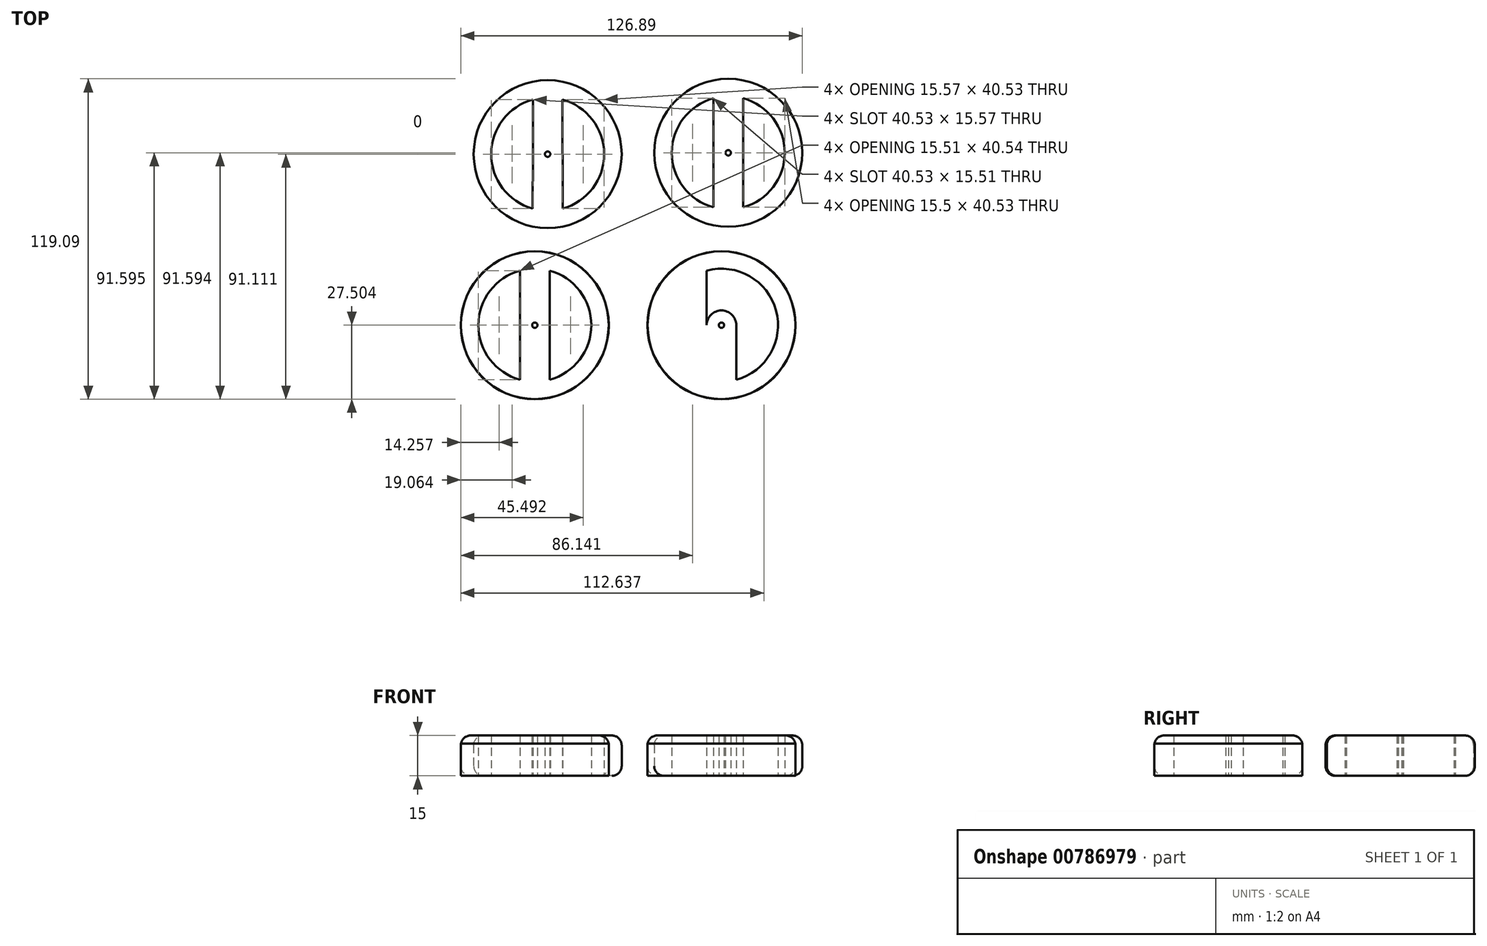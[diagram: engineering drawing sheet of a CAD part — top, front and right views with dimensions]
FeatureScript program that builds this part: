
annotation { "Feature Type Name" : "Feature", "Feature Type Description" : "" }
export const myFeature = defineFeature(function(context is Context, id is Id, definition is map)
    precondition{}
    {
        {
            var Q0;
            Q0=qCreatedBy(makeId("Top.planeOp"),FACE);
            var sketch = newSketch(context, id + "F0", { "sketchPlane" : qUnion([Q0])});
            skCircle(sketch, "E0", {"center": v(-34.05, 31.81) * mm, "radius": 27.5 * mm});
            skCircle(sketch, "E1", {"center": v(33.06, 32.31) * mm, "radius": 27.5 * mm});
            skCircle(sketch, "E2", {"center": v(30.54, -31.78) * mm, "radius": 27.5 * mm});
            skCircle(sketch, "E3", {"center": v(-38.83, -31.78) * mm, "radius": 27.5 * mm});
            skCircle(sketch, "E4", {"center": v(-38.83, -31.78) * mm, "radius": 21 * mm});
            skCircle(sketch, "E5", {"center": v(30.54, -31.78) * mm, "radius": 21 * mm});
            skCircle(sketch, "E6", {"center": v(33.06, 32.31) * mm, "radius": 21 * mm});
            skCircle(sketch, "E7", {"center": v(33.06, 32.31) * mm, "radius": 1 * mm});
            skCircle(sketch, "E8", {"center": v(33.06, 32.31) * mm, "radius": 5.5 * mm});
            skCircle(sketch, "E9", {"center": v(-34.05, 31.81) * mm, "radius": 21 * mm});
            skCircle(sketch, "E10", {"center": v(-34.05, 31.81) * mm, "radius": 5.5 * mm});
            skCircle(sketch, "E11", {"center": v(-38.83, -31.78) * mm, "radius": 1 * mm});
            skCircle(sketch, "E12", {"center": v(-38.83, -31.78) * mm, "radius": 5.5 * mm});
            skCircle(sketch, "E13", {"center": v(30.54, -31.78) * mm, "radius": 1 * mm});
            skCircle(sketch, "E14", {"center": v(30.54, -31.78) * mm, "radius": 5.5 * mm});
            skCircle(sketch, "E15", {"center": v(-34.05, 31.81) * mm, "radius": 1 * mm});
            skLineSegment(sketch, "E16", {"start": v(-39.48, 32.7) * mm, "end": v(-39.48, 52.1) * mm});
            skLineSegment(sketch, "E17", {"start": v(-39.48, 52.1) * mm, "end": v(-39.62, 11.56) * mm});
            skLineSegment(sketch, "E18", {"start": v(-28.48, 11.56) * mm, "end": v(-28.62, 52.1) * mm});
            skLineSegment(sketch, "E19", {"start": v(27.56, 32.58) * mm, "end": v(27.56, 52.58) * mm});
            skLineSegment(sketch, "E20", {"start": v(27.56, 52.58) * mm, "end": v(27.55, 12.05) * mm});
            skLineSegment(sketch, "E21", {"start": v(-44.32, -31.53) * mm, "end": v(-44.32, -11.5) * mm});
            skLineSegment(sketch, "E22", {"start": v(-44.32, -31.53) * mm, "end": v(-44.32, -52.04) * mm});
            skLineSegment(sketch, "E23", {"start": v(-33.33, -31.53) * mm, "end": v(-33.33, -52.04) * mm});
            skLineSegment(sketch, "E24", {"start": v(-33.33, -31.53) * mm, "end": v(-33.33, -11.5) * mm});
            skLineSegment(sketch, "E25", {"start": v(25.04, -31.78) * mm, "end": v(25.04, -11.51) * mm});
            skLineSegment(sketch, "E26", {"start": v(25.04, -11.51) * mm, "end": v(25.04, -52.04) * mm});
            skLineSegment(sketch, "E27", {"start": v(36.04, -31.78) * mm, "end": v(36.04, -11.51) * mm});
            skLineSegment(sketch, "E28", {"start": v(36.04, -11.51) * mm, "end": v(36.04, -52.04) * mm});
            skLineSegment(sketch, "E29", {"start": v(38.56, 32.31) * mm, "end": v(38.56, 12.05) * mm});
            skLineSegment(sketch, "E30", {"start": v(38.56, 32.31) * mm, "end": v(38.56, 52.58) * mm});
            skSolve(sketch);
        }
        {
            var Q0;
            Q0=makeQuery(id+"F0.imprint","IMPRINT",FACE,{"disambiguationData":[TD([[makeQuery(id+"F0.imprint","IMPRINT",EDGE,{"derivedFrom":sQuery(id+"F0.wireOp",EDGE,"E0")}),1.0]])]});
            var Q1;
            Q1=makeQuery(id+"F0.imprint","IMPRINT",FACE,{"disambiguationData":[TD([[makeQuery(id+"F0.imprint","IMPRINT",EDGE,{"derivedFrom":sQuery(id+"F0.wireOp",EDGE,"E1")}),1.0]])]});
            var Q2;
            {var subQ0=sQuery(id+"F0.wireOp",EDGE,"E17");var subQ1=sQuery(id+"F0.wireOp",EDGE,"E9");var subQ2=makeQuery(id+"F0.imprint","INTERSECT",VERTEX,{"derivedFrom":[subQ1,subQ0]});Q2=makeQuery(id+"F0.imprint","IMPRINT",FACE,{"disambiguationData":[TD([[makeQuery(id+"F0.imprint","IMPRINT",EDGE,{"disambiguationData":[TD([[subQ2,-1.0]])],"derivedFrom":subQ1}),1.0]])]});}
            var Q3;
            Q3=makeQuery(id+"F0.imprint","IMPRINT",FACE,{"disambiguationData":[TD([[makeQuery(id+"F0.imprint","IMPRINT",EDGE,{"derivedFrom":sQuery(id+"F0.wireOp",EDGE,"E15")}),-1.0]])]});
            var Q4;
            {var subQ0=sQuery(id+"F0.wireOp",EDGE,"E16");Q4=makeQuery(id+"F0.imprint","IMPRINT",FACE,{"disambiguationData":[TD([[makeQuery(id+"F0.imprint","IMPRINT",EDGE,{"derivedFrom":subQ0}),-1.0]])]});}
            var Q5;
            Q5=makeQuery(id+"F0.imprint","IMPRINT",FACE,{"disambiguationData":[TD([[makeQuery(id+"F0.imprint","IMPRINT",EDGE,{"derivedFrom":sQuery(id+"F0.wireOp",EDGE,"E7")}),-1.0]])]});
            var Q6;
            {var subQ0=sQuery(id+"F0.wireOp",EDGE,"E19");Q6=makeQuery(id+"F0.imprint","IMPRINT",FACE,{"disambiguationData":[TD([[makeQuery(id+"F0.imprint","IMPRINT",EDGE,{"derivedFrom":subQ0}),-1.0]])]});}
            var Q7;
            {var subQ0=sQuery(id+"F0.wireOp",EDGE,"E20");var subQ1=sQuery(id+"F0.wireOp",EDGE,"E6");var subQ2=makeQuery(id+"F0.imprint","INTERSECT",VERTEX,{"derivedFrom":[subQ1,subQ0]});Q7=makeQuery(id+"F0.imprint","IMPRINT",FACE,{"disambiguationData":[TD([[makeQuery(id+"F0.imprint","IMPRINT",EDGE,{"disambiguationData":[TD([[subQ2,-1.0]])],"derivedFrom":subQ1}),1.0]])]});}
            extrude(context, id + "F1", {"entities" : qUnion([Q0, Q1, Q2, Q3, Q4, Q5, Q6, Q7]), "depth" : 15 * mm, "offsetDistance" : 25 * mm});
        }
        {
            var Q0;
            Q0=makeQuery(id+"F1.opExtrude","CAP_EDGE",EDGE,{"disambiguationData":[OSD([sQuery(id+"F0.wireOp",EDGE,"E0")])],"isStart":false});
            var Q1;
            Q1=makeQuery(id+"F1.opExtrude","CAP_EDGE",EDGE,{"disambiguationData":[OSD([sQuery(id+"F0.wireOp",EDGE,"E0")])],"isStart":true});
            fillet(context, id + "F2", {"entities" : qUnion([Q0, Q1]), "radius" : 3.62 * mm, "tangentPropagation" : true, "allowEdgeOverflow" : false});
        }
        {
            var Q0;
            Q0=makeQuery(id+"F1.opExtrude","CAP_EDGE",EDGE,{"disambiguationData":[OSD([sQuery(id+"F0.wireOp",EDGE,"E1")])],"isStart":false});
            var Q1;
            Q1=makeQuery(id+"F1.opExtrude","CAP_EDGE",EDGE,{"disambiguationData":[OSD([sQuery(id+"F0.wireOp",EDGE,"E1")])],"isStart":true});
            fillet(context, id + "F3", {"entities" : qUnion([Q0, Q1]), "radius" : 3.62 * mm, "tangentPropagation" : true, "allowEdgeOverflow" : false});
        }
        {
            var Q0;
            {var subQ0=sQuery(id+"F0.wireOp",EDGE,"E26");var subQ1=sQuery(id+"F0.wireOp",EDGE,"E5");var subQ2=makeQuery(id+"F0.imprint","INTERSECT",VERTEX,{"disambiguationData":[OD(0.0)],"derivedFrom":[subQ1,subQ0]});Q0=makeQuery(id+"F0.imprint","IMPRINT",FACE,{"disambiguationData":[TD([[makeQuery(id+"F0.imprint","IMPRINT",EDGE,{"disambiguationData":[TD([[subQ2,1.0]])],"derivedFrom":subQ1}),1.0]])]});}
            var Q1;
            {var subQ0=sQuery(id+"F0.wireOp",EDGE,"E26");var subQ1=sQuery(id+"F0.wireOp",EDGE,"E5");var subQ2=makeQuery(id+"F0.imprint","INTERSECT",VERTEX,{"disambiguationData":[OD(1.0)],"derivedFrom":[subQ1,subQ0]});Q1=makeQuery(id+"F0.imprint","IMPRINT",FACE,{"disambiguationData":[TD([[makeQuery(id+"F0.imprint","IMPRINT",EDGE,{"disambiguationData":[TD([[subQ2,-1.0]])],"derivedFrom":subQ1}),1.0]])]});}
            var Q2;
            Q2=makeQuery(id+"F0.imprint","IMPRINT",FACE,{"disambiguationData":[TD([[makeQuery(id+"F0.imprint","IMPRINT",EDGE,{"derivedFrom":sQuery(id+"F0.wireOp",EDGE,"E13")}),-1.0]])]});
            var Q3;
            Q3=makeQuery(id+"F0.imprint","IMPRINT",FACE,{"disambiguationData":[TD([[makeQuery(id+"F0.imprint","IMPRINT",EDGE,{"derivedFrom":sQuery(id+"F0.wireOp",EDGE,"E2")}),1.0]])]});
            var Q4;
            {var subQ0=sQuery(id+"F0.wireOp",EDGE,"E22");var subQ1=sQuery(id+"F0.wireOp",EDGE,"E4");var subQ2=makeQuery(id+"F0.imprint","INTERSECT",VERTEX,{"derivedFrom":[subQ1,subQ0]});Q4=makeQuery(id+"F0.imprint","IMPRINT",FACE,{"disambiguationData":[TD([[makeQuery(id+"F0.imprint","IMPRINT",EDGE,{"disambiguationData":[TD([[subQ2,-1.0]])],"derivedFrom":subQ1}),1.0]])]});}
            var Q5;
            Q5=makeQuery(id+"F0.imprint","IMPRINT",FACE,{"disambiguationData":[TD([[makeQuery(id+"F0.imprint","IMPRINT",EDGE,{"derivedFrom":sQuery(id+"F0.wireOp",EDGE,"E11")}),-1.0]])]});
            var Q6;
            {var subQ0=sQuery(id+"F0.wireOp",EDGE,"E21");Q6=makeQuery(id+"F0.imprint","IMPRINT",FACE,{"disambiguationData":[TD([[makeQuery(id+"F0.imprint","IMPRINT",EDGE,{"derivedFrom":subQ0}),-1.0]])]});}
            var Q7;
            Q7=makeQuery(id+"F0.imprint","IMPRINT",FACE,{"disambiguationData":[TD([[makeQuery(id+"F0.imprint","IMPRINT",EDGE,{"derivedFrom":sQuery(id+"F0.wireOp",EDGE,"E3")}),1.0]])]});
            extrude(context, id + "F4", {"entities" : qUnion([Q0, Q1, Q2, Q3, Q4, Q5, Q6, Q7]), "operationType" : NewBodyOperationType.ADD, "depth" : 12 * mm, "offsetDistance" : 25 * mm});
        }
        {
            var Q0;
            Q0=makeQuery(id+"F0.imprint","IMPRINT",FACE,{"disambiguationData":[TD([[makeQuery(id+"F0.imprint","IMPRINT",EDGE,{"derivedFrom":sQuery(id+"F0.wireOp",EDGE,"E2")}),1.0]])]});
            var Q1;
            {var subQ0=sQuery(id+"F0.wireOp",EDGE,"E26");var subQ1=sQuery(id+"F0.wireOp",EDGE,"E5");var subQ2=makeQuery(id+"F0.imprint","INTERSECT",VERTEX,{"disambiguationData":[OD(1.0)],"derivedFrom":[subQ1,subQ0]});Q1=makeQuery(id+"F0.imprint","IMPRINT",FACE,{"disambiguationData":[TD([[makeQuery(id+"F0.imprint","IMPRINT",EDGE,{"disambiguationData":[TD([[subQ2,-1.0]])],"derivedFrom":subQ1}),1.0]])]});}
            var Q2;
            Q2=makeQuery(id+"F0.imprint","IMPRINT",FACE,{"disambiguationData":[TD([[makeQuery(id+"F0.imprint","IMPRINT",EDGE,{"derivedFrom":sQuery(id+"F0.wireOp",EDGE,"E13")}),-1.0]])]});
            var Q3;
            {var subQ0=sQuery(id+"F0.wireOp",EDGE,"E26");var subQ1=sQuery(id+"F0.wireOp",EDGE,"E5");var subQ2=makeQuery(id+"F0.imprint","INTERSECT",VERTEX,{"disambiguationData":[OD(0.0)],"derivedFrom":[subQ1,subQ0]});Q3=makeQuery(id+"F0.imprint","IMPRINT",FACE,{"disambiguationData":[TD([[makeQuery(id+"F0.imprint","IMPRINT",EDGE,{"disambiguationData":[TD([[subQ2,1.0]])],"derivedFrom":subQ1}),1.0]])]});}
            var Q4;
            {var subQ0=sQuery(id+"F0.wireOp",EDGE,"E21");Q4=makeQuery(id+"F0.imprint","IMPRINT",FACE,{"disambiguationData":[TD([[makeQuery(id+"F0.imprint","IMPRINT",EDGE,{"derivedFrom":subQ0}),-1.0]])]});}
            var Q5;
            Q5=makeQuery(id+"F0.imprint","IMPRINT",FACE,{"disambiguationData":[TD([[makeQuery(id+"F0.imprint","IMPRINT",EDGE,{"derivedFrom":sQuery(id+"F0.wireOp",EDGE,"E3")}),1.0]])]});
            var Q6;
            Q6=makeQuery(id+"F0.imprint","IMPRINT",FACE,{"disambiguationData":[TD([[makeQuery(id+"F0.imprint","IMPRINT",EDGE,{"derivedFrom":sQuery(id+"F0.wireOp",EDGE,"E11")}),-1.0]])]});
            var Q7;
            {var subQ0=sQuery(id+"F0.wireOp",EDGE,"E22");var subQ1=sQuery(id+"F0.wireOp",EDGE,"E4");var subQ2=makeQuery(id+"F0.imprint","INTERSECT",VERTEX,{"derivedFrom":[subQ1,subQ0]});Q7=makeQuery(id+"F0.imprint","IMPRINT",FACE,{"disambiguationData":[TD([[makeQuery(id+"F0.imprint","IMPRINT",EDGE,{"disambiguationData":[TD([[subQ2,-1.0]])],"derivedFrom":subQ1}),1.0]])]});}
            extrude(context, id + "F5", {"entities" : qUnion([Q0, Q1, Q2, Q3, Q4, Q5, Q6, Q7]), "depth" : 15 * mm, "offsetDistance" : 25 * mm});
        }
        {
            var Q0;
            Q0=makeQuery(id+"F5.opExtrude","CAP_EDGE",EDGE,{"disambiguationData":[OSD([sQuery(id+"F0.wireOp",EDGE,"E3")])],"isStart":false});
            var Q1;
            Q1=makeQuery(id+"F5.opExtrude","CAP_EDGE",EDGE,{"disambiguationData":[OSD([sQuery(id+"F0.wireOp",EDGE,"E3")])],"isStart":true});
            fillet(context, id + "F6", {"entities" : qUnion([Q0, Q1]), "radius" : 3.62 * mm, "tangentPropagation" : true, "allowEdgeOverflow" : false});
        }
        {
            var Q0;
            Q0=makeQuery(id+"F5.opExtrude","CAP_EDGE",EDGE,{"disambiguationData":[OSD([sQuery(id+"F0.wireOp",EDGE,"E2")])],"isStart":false});
            var Q1;
            Q1=makeQuery(id+"F5.opExtrude","CAP_EDGE",EDGE,{"disambiguationData":[OSD([sQuery(id+"F0.wireOp",EDGE,"E2")])],"isStart":true});
            fillet(context, id + "F7", {"entities" : qUnion([Q0, Q1]), "radius" : 3.62 * mm, "tangentPropagation" : true, "allowEdgeOverflow" : false});
        }
    });
